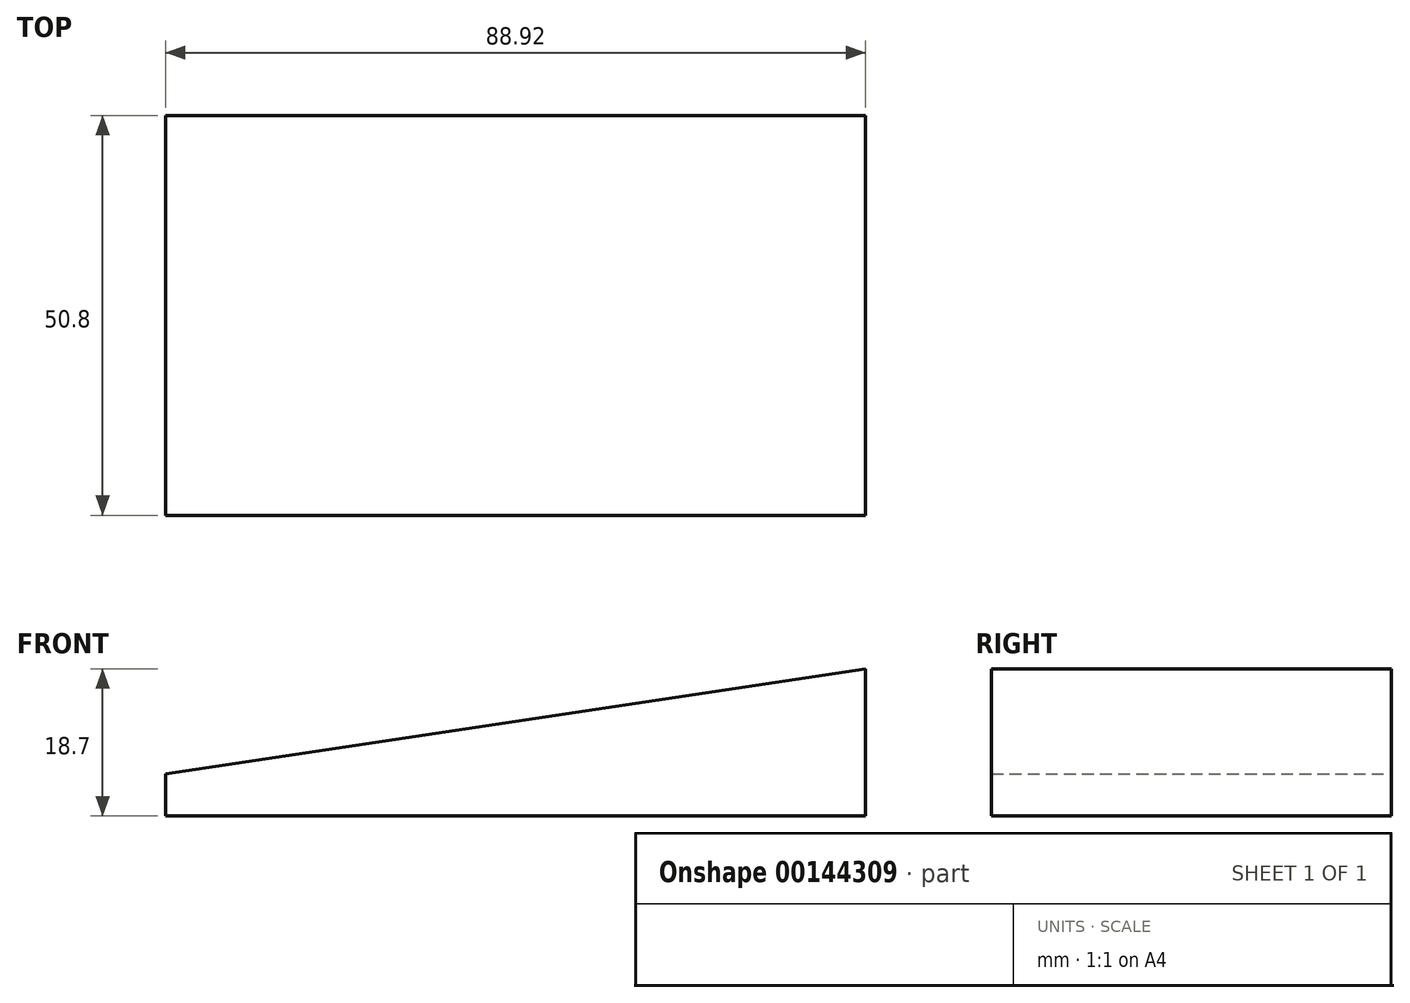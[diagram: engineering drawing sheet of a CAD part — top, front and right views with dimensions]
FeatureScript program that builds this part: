
annotation { "Feature Type Name" : "Feature", "Feature Type Description" : "" }
export const myFeature = defineFeature(function(context is Context, id is Id, definition is map)
    precondition{}
    {
        {
            var Q0;
            Q0=qCreatedBy(makeId("Front.planeOp"),FACE);
            var sketch = newSketch(context, id + "F0", { "sketchPlane" : qUnion([Q0])});
            skLineSegment(sketch, "E0", {"start": v(0, 0) * mm, "end": v(88.92, 0) * mm});
            skLineSegment(sketch, "E1", {"start": v(88.92, 0) * mm, "end": v(88.92, 18.7) * mm});
            skLineSegment(sketch, "E2", {"start": v(88.92, 18.7) * mm, "end": v(0, 5.39) * mm});
            skLineSegment(sketch, "E3", {"start": v(0, 5.39) * mm, "end": v(0, 0) * mm});
            skSolve(sketch);
        }
        {
            var Q0;
            Q0 = qSketchRegion(id + "F0", true);
            extrude(context, id + "F1", {"entities" : qUnion([Q0]), "endBound" : BoundingType.SYMMETRIC, "depth" : 50.8 * mm});
        }
    });
